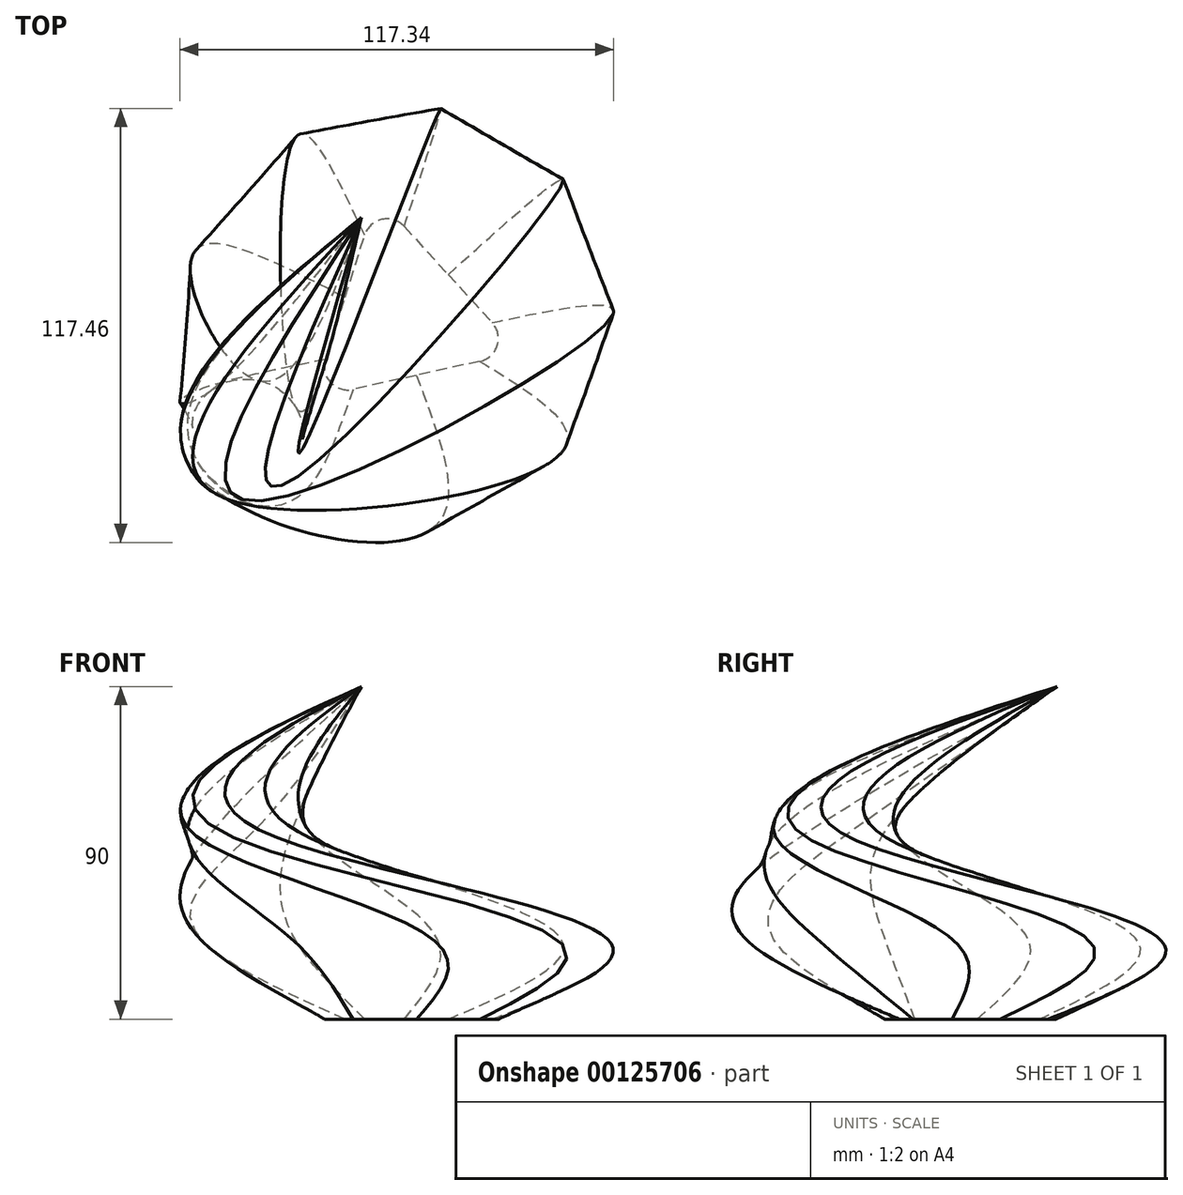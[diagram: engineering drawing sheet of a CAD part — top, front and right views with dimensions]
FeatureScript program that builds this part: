
annotation { "Feature Type Name" : "Feature", "Feature Type Description" : "" }
export const myFeature = defineFeature(function(context is Context, id is Id, definition is map)
    precondition{}
    {
        {
            var Q0;
            Q0=qCreatedBy(makeId("Top.planeOp"),FACE);
            cPlane(context, id + "F0", {"entities" : qUnion([Q0]), "cplaneType" : CPlaneType.OFFSET, "offset" : 20 * mm, "width" : 152.4 * mm, "height" : 152.4 * mm});
        }
        {
            var Q0;
            Q0=qCreatedBy(makeId("Top.planeOp"),FACE);
            cPlane(context, id + "F1", {"entities" : qUnion([Q0]), "cplaneType" : CPlaneType.OFFSET, "offset" : 50 * mm, "width" : 152.4 * mm, "height" : 152.4 * mm});
        }
        {
            var Q0;
            Q0=qCreatedBy(makeId("Top.planeOp"),FACE);
            cPlane(context, id + "F2", {"entities" : qUnion([Q0]), "cplaneType" : CPlaneType.OFFSET, "offset" : 90 * mm, "width" : 152.4 * mm, "height" : 152.4 * mm});
        }
        {
            var Q0;
            Q0=qCreatedBy(makeId("Top.planeOp"),FACE);
            var sketch = newSketch(context, id + "F3", { "sketchPlane" : qUnion([Q0])});
            skCircle(sketch, "E0.cCircle", {"center": v(0, 0) * mm, "radius": 33.04 * mm, "construction": true});
            skLineSegment(sketch, "E0.0", {"start": v(-21.05, -11.83) * mm, "end": v(-10.45, 21.77) * mm});
            skLineSegment(sketch, "E0.1", {"start": v(0.29, 24.15) * mm, "end": v(24.08, -1.83) * mm});
            skLineSegment(sketch, "E0.2", {"start": v(20.77, -12.32) * mm, "end": v(-13.63, -19.94) * mm});
            skPoint(sketch, "E1.visualSharp", {"position": v(-7.14, 32.26) * mm});
            skArc(sketch, "E1.filletArc", {"start": v(0.29, 24.15) * mm, "mid": v(-5.77, 26.06) * mm, "end": v(-10.45, 21.77) * mm});
            skPoint(sketch, "E2.visualSharp", {"position": v(-24.36, -22.32) * mm});
            skArc(sketch, "E2.filletArc", {"start": v(-21.05, -11.83) * mm, "mid": v(-19.68, -18.03) * mm, "end": v(-13.63, -19.94) * mm});
            skPoint(sketch, "E3.visualSharp", {"position": v(31.5, -9.94) * mm});
            skArc(sketch, "E3.filletArc", {"start": v(20.77, -12.32) * mm, "mid": v(25.45, -8.03) * mm, "end": v(24.08, -1.83) * mm});
            skSolve(sketch);
        }
        {
            var Q0;
            Q0=qCreatedBy(id+"F0.planeOp",FACE);
            var sketch = newSketch(context, id + "F4", { "sketchPlane" : qUnion([Q0])});
            skCircle(sketch, "E4.cCircle", {"center": v(0, 0) * mm, "radius": 53.18 * mm, "construction": true});
            skLineSegment(sketch, "E4.0", {"start": v(-28.33, -49) * mm, "end": v(-53.2, -19.32) * mm});
            skLineSegment(sketch, "E4.1", {"start": v(-53.2, -19.32) * mm, "end": v(-53.17, 19.4) * mm});
            skLineSegment(sketch, "E4.2", {"start": v(-53.17, 19.4) * mm, "end": v(-28.26, 49.03) * mm});
            skLineSegment(sketch, "E4.3", {"start": v(-28.26, 49.03) * mm, "end": v(9.86, 55.73) * mm});
            skLineSegment(sketch, "E4.4", {"start": v(9.86, 55.73) * mm, "end": v(43.38, 36.35) * mm});
            skLineSegment(sketch, "E4.5", {"start": v(43.38, 36.35) * mm, "end": v(56.6, -0.04) * mm});
            skLineSegment(sketch, "E4.6", {"start": v(56.6, -0.04) * mm, "end": v(43.33, -36.4) * mm});
            skLineSegment(sketch, "E4.7", {"start": v(43.33, -36.4) * mm, "end": v(9.8, -55.74) * mm});
            skLineSegment(sketch, "E4.8", {"start": v(9.8, -55.74) * mm, "end": v(-28.33, -49) * mm});
            skPoint(sketch, "E4.0.midPoint", {"position": v(-40.76, -34.16) * mm});
            skSolve(sketch);
        }
        {
            var Q0;
            Q0=qCreatedBy(id+"F1.planeOp",FACE);
            var sketch = newSketch(context, id + "F5", { "sketchPlane" : qUnion([Q0])});
            skCircle(sketch, "E5", {"center": v(-41.67, -33.7) * mm, "radius": 17 * mm});
            skCircle(sketch, "E6", {"center": v(43.5, 35.98) * mm, "radius": 19.84 * mm});
            skSolve(sketch);
        }
        {
            var Q0;
            Q0=qCreatedBy(id+"F2.planeOp",FACE);
            var sketch = newSketch(context, id + "F6", { "sketchPlane" : qUnion([Q0])});
            skCircle(sketch, "E7.cCircle", {"center": v(0, 0) * mm, "radius": 28.85 * mm, "construction": true});
            skLineSegment(sketch, "E7.0", {"start": v(-9.95, -27.14) * mm, "end": v(-13.27, -25.68) * mm});
            skLineSegment(sketch, "E7.1", {"start": v(-13.27, -25.68) * mm, "end": v(-16.39, -23.82) * mm});
            skLineSegment(sketch, "E7.2", {"start": v(-16.39, -23.82) * mm, "end": v(-19.24, -21.58) * mm});
            skLineSegment(sketch, "E7.3", {"start": v(-19.24, -21.58) * mm, "end": v(-21.8, -19) * mm});
            skLineSegment(sketch, "E7.4", {"start": v(-21.8, -19) * mm, "end": v(-24, -16.11) * mm});
            skLineSegment(sketch, "E7.5", {"start": v(-24, -16.11) * mm, "end": v(-25.84, -12.98) * mm});
            skLineSegment(sketch, "E7.6", {"start": v(-25.84, -12.98) * mm, "end": v(-27.26, -9.64) * mm});
            skLineSegment(sketch, "E7.7", {"start": v(-27.26, -9.64) * mm, "end": v(-28.25, -6.14) * mm});
            skLineSegment(sketch, "E7.8", {"start": v(-28.25, -6.14) * mm, "end": v(-28.8, -2.55) * mm});
            skLineSegment(sketch, "E7.9", {"start": v(-28.8, -2.55) * mm, "end": v(-28.9, 1.08) * mm});
            skLineSegment(sketch, "E7.10", {"start": v(-28.9, 1.08) * mm, "end": v(-28.53, 4.69) * mm});
            skLineSegment(sketch, "E7.11", {"start": v(-28.53, 4.69) * mm, "end": v(-27.72, 8.23) * mm});
            skLineSegment(sketch, "E7.12", {"start": v(-27.72, 8.23) * mm, "end": v(-26.47, 11.64) * mm});
            skLineSegment(sketch, "E7.13", {"start": v(-26.47, 11.64) * mm, "end": v(-24.8, 14.86) * mm});
            skLineSegment(sketch, "E7.14", {"start": v(-24.8, 14.86) * mm, "end": v(-22.74, 17.85) * mm});
            skLineSegment(sketch, "E7.15", {"start": v(-22.74, 17.85) * mm, "end": v(-20.32, 20.56) * mm});
            skLineSegment(sketch, "E7.16", {"start": v(-20.32, 20.56) * mm, "end": v(-17.59, 22.95) * mm});
            skLineSegment(sketch, "E7.17", {"start": v(-17.59, 22.95) * mm, "end": v(-14.57, 24.97) * mm});
            skLineSegment(sketch, "E7.18", {"start": v(-14.57, 24.97) * mm, "end": v(-11.33, 26.6) * mm});
            skLineSegment(sketch, "E7.19", {"start": v(-11.33, 26.6) * mm, "end": v(-7.9, 27.8) * mm});
            skLineSegment(sketch, "E7.20", {"start": v(-7.9, 27.8) * mm, "end": v(-4.36, 28.58) * mm});
            skLineSegment(sketch, "E7.21", {"start": v(-4.36, 28.58) * mm, "end": v(-0.74, 28.9) * mm});
            skLineSegment(sketch, "E7.22", {"start": v(-0.74, 28.9) * mm, "end": v(2.89, 28.77) * mm});
            skLineSegment(sketch, "E7.23", {"start": v(2.89, 28.77) * mm, "end": v(6.47, 28.18) * mm});
            skLineSegment(sketch, "E7.24", {"start": v(6.47, 28.18) * mm, "end": v(9.95, 27.14) * mm});
            skLineSegment(sketch, "E7.25", {"start": v(9.95, 27.14) * mm, "end": v(13.27, 25.68) * mm});
            skLineSegment(sketch, "E7.26", {"start": v(13.27, 25.68) * mm, "end": v(16.39, 23.82) * mm});
            skLineSegment(sketch, "E7.27", {"start": v(16.39, 23.82) * mm, "end": v(19.24, 21.58) * mm});
            skLineSegment(sketch, "E7.28", {"start": v(19.24, 21.58) * mm, "end": v(21.8, 19) * mm});
            skLineSegment(sketch, "E7.29", {"start": v(21.8, 19) * mm, "end": v(24, 16.11) * mm});
            skLineSegment(sketch, "E7.30", {"start": v(24, 16.11) * mm, "end": v(25.84, 12.98) * mm});
            skLineSegment(sketch, "E7.31", {"start": v(25.84, 12.98) * mm, "end": v(27.26, 9.64) * mm});
            skLineSegment(sketch, "E7.32", {"start": v(27.26, 9.64) * mm, "end": v(28.25, 6.14) * mm});
            skLineSegment(sketch, "E7.33", {"start": v(28.25, 6.14) * mm, "end": v(28.8, 2.55) * mm});
            skLineSegment(sketch, "E7.34", {"start": v(28.8, 2.55) * mm, "end": v(28.9, -1.08) * mm});
            skLineSegment(sketch, "E7.35", {"start": v(28.9, -1.08) * mm, "end": v(28.53, -4.69) * mm});
            skLineSegment(sketch, "E7.36", {"start": v(28.53, -4.69) * mm, "end": v(27.72, -8.23) * mm});
            skLineSegment(sketch, "E7.37", {"start": v(27.72, -8.23) * mm, "end": v(26.47, -11.64) * mm});
            skLineSegment(sketch, "E7.38", {"start": v(26.47, -11.64) * mm, "end": v(24.8, -14.86) * mm});
            skLineSegment(sketch, "E7.39", {"start": v(24.8, -14.86) * mm, "end": v(22.74, -17.85) * mm});
            skLineSegment(sketch, "E7.40", {"start": v(22.74, -17.85) * mm, "end": v(20.32, -20.56) * mm});
            skLineSegment(sketch, "E7.41", {"start": v(20.32, -20.56) * mm, "end": v(17.59, -22.95) * mm});
            skLineSegment(sketch, "E7.42", {"start": v(17.59, -22.95) * mm, "end": v(14.57, -24.97) * mm});
            skLineSegment(sketch, "E7.43", {"start": v(14.57, -24.97) * mm, "end": v(11.33, -26.6) * mm});
            skLineSegment(sketch, "E7.44", {"start": v(11.33, -26.6) * mm, "end": v(7.9, -27.8) * mm});
            skLineSegment(sketch, "E7.45", {"start": v(7.9, -27.8) * mm, "end": v(4.36, -28.58) * mm});
            skLineSegment(sketch, "E7.46", {"start": v(4.36, -28.58) * mm, "end": v(0.74, -28.9) * mm});
            skLineSegment(sketch, "E7.47", {"start": v(0.74, -28.9) * mm, "end": v(-2.89, -28.77) * mm});
            skLineSegment(sketch, "E7.48", {"start": v(-2.89, -28.77) * mm, "end": v(-6.47, -28.18) * mm});
            skLineSegment(sketch, "E7.49", {"start": v(-6.47, -28.18) * mm, "end": v(-9.95, -27.14) * mm});
            skPoint(sketch, "E7.0.midPoint", {"position": v(-11.61, -26.41) * mm});
            skSolve(sketch);
        }
        {
            var Q0;
            Q0=makeQuery(id+"F3.imprint","IMPRINT",FACE,{"disambiguationData":[TD([[makeQuery(id+"F3.imprint","IMPRINT",EDGE,{"derivedFrom":sQuery(id+"F3.wireOp",EDGE,"E0.0")}),-1.0]])]});
            var Q1;
            Q1=makeQuery(id+"F4.imprint","IMPRINT",FACE,{"disambiguationData":[TD([[makeQuery(id+"F4.imprint","IMPRINT",EDGE,{"derivedFrom":sQuery(id+"F4.wireOp",EDGE,"E4.0")}),-1.0]])]});
            var Q2;
            Q2=makeQuery(id+"F5.imprint","IMPRINT",FACE,{"disambiguationData":[TD([[makeQuery(id+"F5.imprint","IMPRINT",EDGE,{"derivedFrom":sQuery(id+"F5.wireOp",EDGE,"E5")}),1.0]])]});
            var Q3;
            Q3=sQuery(id+"F6.wireOp",VERTEX,"E7.19.start");
            loft(context, id + "F7", {"sheetProfilesArray" : [{ "sheetProfileEntities" : qUnion([Q0]) }, { "sheetProfileEntities" : qUnion([Q1]) }, { "sheetProfileEntities" : qUnion([Q2]) }, { "sheetProfileEntities" : qUnion([Q3]) }]});
        }
    });
